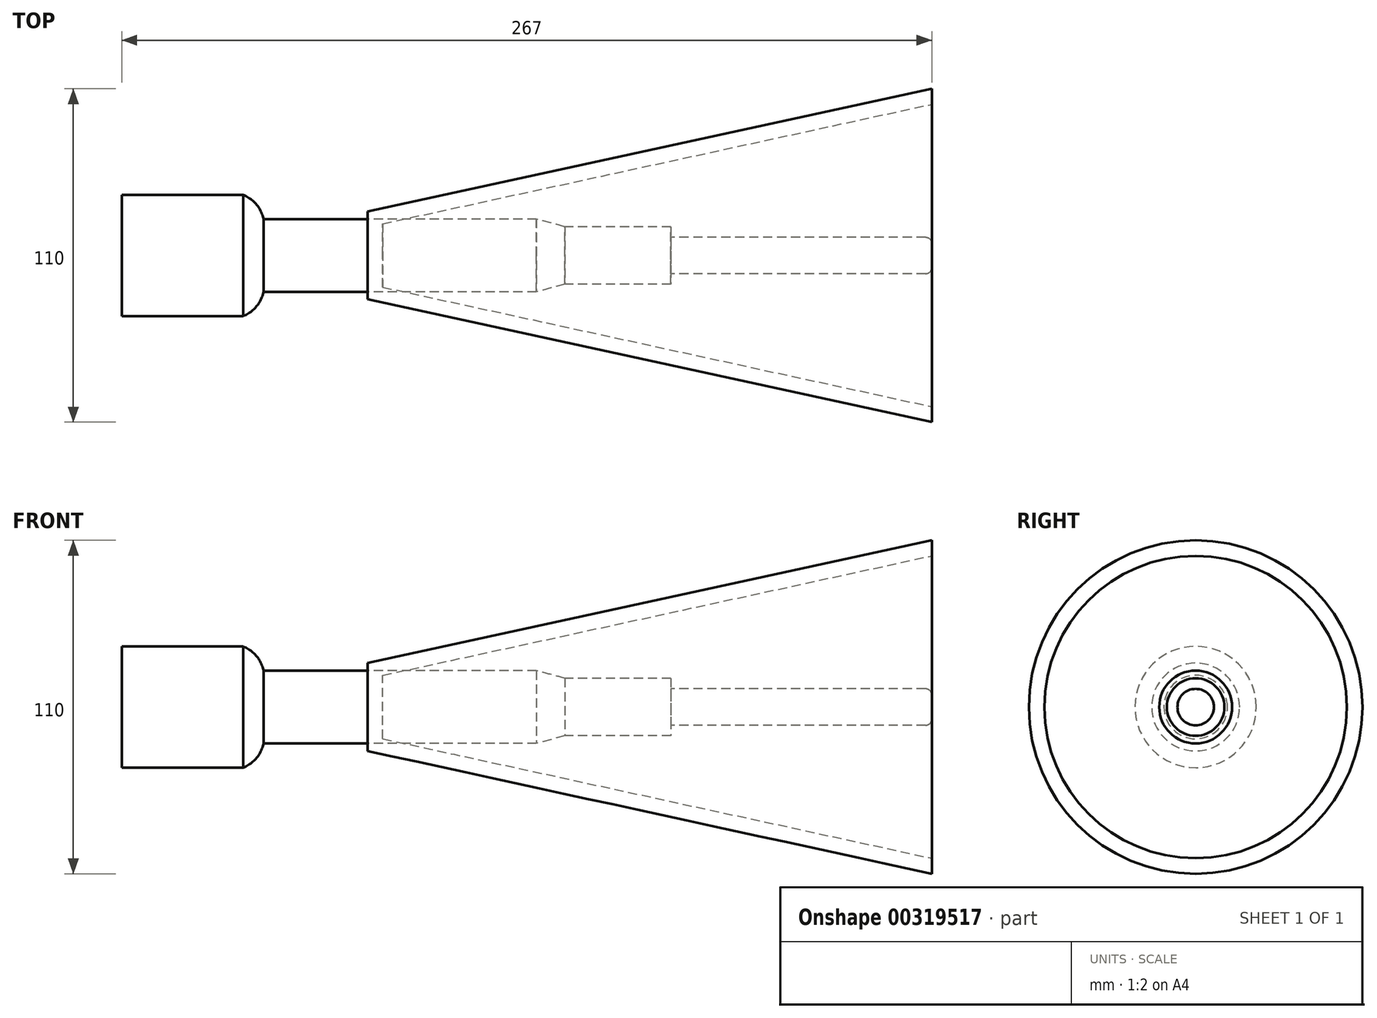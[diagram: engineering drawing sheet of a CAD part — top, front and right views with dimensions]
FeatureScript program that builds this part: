
annotation { "Feature Type Name" : "Feature", "Feature Type Description" : "" }
export const myFeature = defineFeature(function(context is Context, id is Id, definition is map)
    precondition{}
    {
        {
            var Q0;
            Q0=qCreatedBy(makeId("Front.planeOp"),FACE);
            var sketch = newSketch(context, id + "F0", { "sketchPlane" : qUnion([Q0])});
            skLineSegment(sketch, "E0", {"start": v(0, 0) * mm, "end": v(267, 0) * mm, "construction": true});
            skLineSegment(sketch, "E1", {"start": v(267, 0) * mm, "end": v(267, 6) * mm});
            skLineSegment(sketch, "E2", {"start": v(267, 6) * mm, "end": v(181, 6) * mm});
            skLineSegment(sketch, "E3", {"start": v(181, 6) * mm, "end": v(181, 9.5) * mm});
            skLineSegment(sketch, "E4", {"start": v(181, 9.5) * mm, "end": v(146, 9.5) * mm});
            skLineSegment(sketch, "E5", {"start": v(0, 0) * mm, "end": v(0, 20) * mm});
            skLineSegment(sketch, "E6", {"start": v(0, 20) * mm, "end": v(40, 20) * mm});
            skLineSegment(sketch, "E7", {"start": v(146, 9.5) * mm, "end": v(136.67, 12) * mm});
            skLineSegment(sketch, "E8", {"start": v(136.67, 12) * mm, "end": v(46.67, 12) * mm});
            skArc(sketch, "E9", {"start": v(46.67, 12) * mm, "mid": v(44.34, 16.84) * mm, "end": v(40, 20) * mm});
            skLineSegment(sketch, "E10", {"start": v(0, 0) * mm, "end": v(267, 0) * mm});
            skSolve(sketch);
        }
        {
            var Q0;
            Q0=makeQuery(id+"F0.imprint","IMPRINT",FACE,{"disambiguationData":[TD([[makeQuery(id+"F0.imprint","IMPRINT",EDGE,{"derivedFrom":sQuery(id+"F0.wireOp",EDGE,"E1")}),1.0]])]});
            var Q1;
            Q1=sQuery(id+"F0.wireOp",EDGE,"E10");
            revolve(context, id + "F1", {"entities" : qUnion([Q0]), "axis" : qUnion([Q1]), "revolveType" : RevolveType.FULL});
        }
        {
            var Q0;
            Q0=makeQuery(id+"F1.opRevolve","SWEPT_EDGE",EDGE,{"disambiguationData":[OSD([sQuery(id+"F0.wireOp",EDGE,"E1"),sQuery(id+"F0.wireOp",EDGE,"E2")])]});
            fillet(context, id + "F2", {"entities" : qUnion([Q0]), "radius" : 2 * mm, "tangentPropagation" : true, "allowEdgeOverflow" : false});
        }
        {
            var Q0;
            Q0=makeQuery(id+"F1.opRevolve","SWEPT_FACE",FACE,{"disambiguationData":[OSD([sQuery(id+"F0.wireOp",EDGE,"E3")])]});
            cPlane(context, id + "F3", {"entities" : qUnion([Q0]), "cplaneType" : CPlaneType.OFFSET, "offset" : 100 * mm, "oppositeDirection" : true, "width" : 150 * mm, "height" : 150 * mm});
        }
        {
            var Q0;
            Q0=qCreatedBy(id+"F3.planeOp",FACE);
            var sketch = newSketch(context, id + "F4", { "sketchPlane" : qUnion([Q0])});
            skCircle(sketch, "E11.0", {"center": v(0, 0) * mm, "radius": 12 * mm, "construction": true});
            skCircle(sketch, "E12.0", {"center": v(0, 0) * mm, "radius": 4 * mm, "construction": true});
            skCircle(sketch, "E13", {"center": v(0, 0) * mm, "radius": 14.5 * mm});
            skSolve(sketch);
        }
        {
            var Q0;
            Q0=makeQuery(id+"F1.opRevolve","SWEPT_FACE",FACE,{"disambiguationData":[OSD([sQuery(id+"F0.wireOp",EDGE,"E1")])]});
            cPlane(context, id + "F5", {"entities" : qUnion([Q0]), "cplaneType" : CPlaneType.OFFSET, "offset" : 0 * mm, "width" : 150 * mm, "height" : 150 * mm});
        }
        {
            var Q0;
            Q0=qCreatedBy(id+"F5.planeOp",FACE);
            var sketch = newSketch(context, id + "F6", { "sketchPlane" : qUnion([Q0])});
            skCircle(sketch, "E14.0", {"center": v(0, 0) * mm, "radius": 4 * mm, "construction": true});
            skCircle(sketch, "E15", {"center": v(0, 0) * mm, "radius": 55 * mm});
            skSolve(sketch);
        }
        {
            var Q1;
            Q1=makeQuery(id+"F4.imprint","IMPRINT",FACE,{"disambiguationData":[TD([[makeQuery(id+"F4.imprint","IMPRINT",EDGE,{"derivedFrom":sQuery(id+"F4.wireOp",EDGE,"E13")}),1.0]])]});
            var Q2;
            Q2=makeQuery(id+"F6.imprint","IMPRINT",FACE,{"disambiguationData":[TD([[makeQuery(id+"F6.imprint","IMPRINT",EDGE,{"derivedFrom":sQuery(id+"F6.wireOp",EDGE,"E15")}),1.0]])]});
            loft(context, id + "F7", {"sheetProfilesArray" : [{ "sheetProfileEntities" : qUnion([Q1]) }, { "sheetProfileEntities" : qUnion([Q2]) }]});
        }
        {
            var Q0;
            Q0=makeQuery(id+"F7.opLoft","CAP_FACE",FACE,{"disambiguationData":[OSD([makeQuery(id+"F6.imprint","IMPRINT",FACE,{"disambiguationData":[TD([[makeQuery(id+"F6.imprint","IMPRINT",EDGE,{"derivedFrom":sQuery(id+"F6.wireOp",EDGE,"E15")}),1.0]])]})])],"isStart":true});
            shell(context, id + "F8", {"entities" : qUnion([Q0]), "thickness" : 5 * mm});
        }
    });
